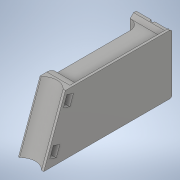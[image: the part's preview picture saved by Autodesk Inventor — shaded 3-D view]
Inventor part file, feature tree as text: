
AUTODESK INVENTOR PART (.ipt)
format: ipt  version: 2021.1 (Build 251245010, 245A)  size: 145,408 bytes
history: mixed  units: in
note: dims shown in document units (in); Inventor stores cm internally (conversion verified against a paired STEP export)
features: extrude x1, sketch x1, imported_body x1
ambient origin geometry x8: Origin, YZ Plane, XZ Plane, XY Plane, X Axis, Y Axis, Z Axis, Center Point
bodies: Solid1 (imported_parasolid), Body1 (imported_parasolid)
feature tree (3):
  extrude  "Extrusion2"  [1 undecoded]
  sketch  "Skizze2"  dims[d2=0.0in d3=0.0in]
  imported_body  NMx_Import_Brep_tag  [imported B-rep: ~40 faces, bbox_mm=[31.0, 51.6, 111.280864]]
note: 1 required parameter value undecoded (feature->parameter linkage not recoverable at this tier; creation-order binding heuristic only, values carry confidence <= 0.55)
